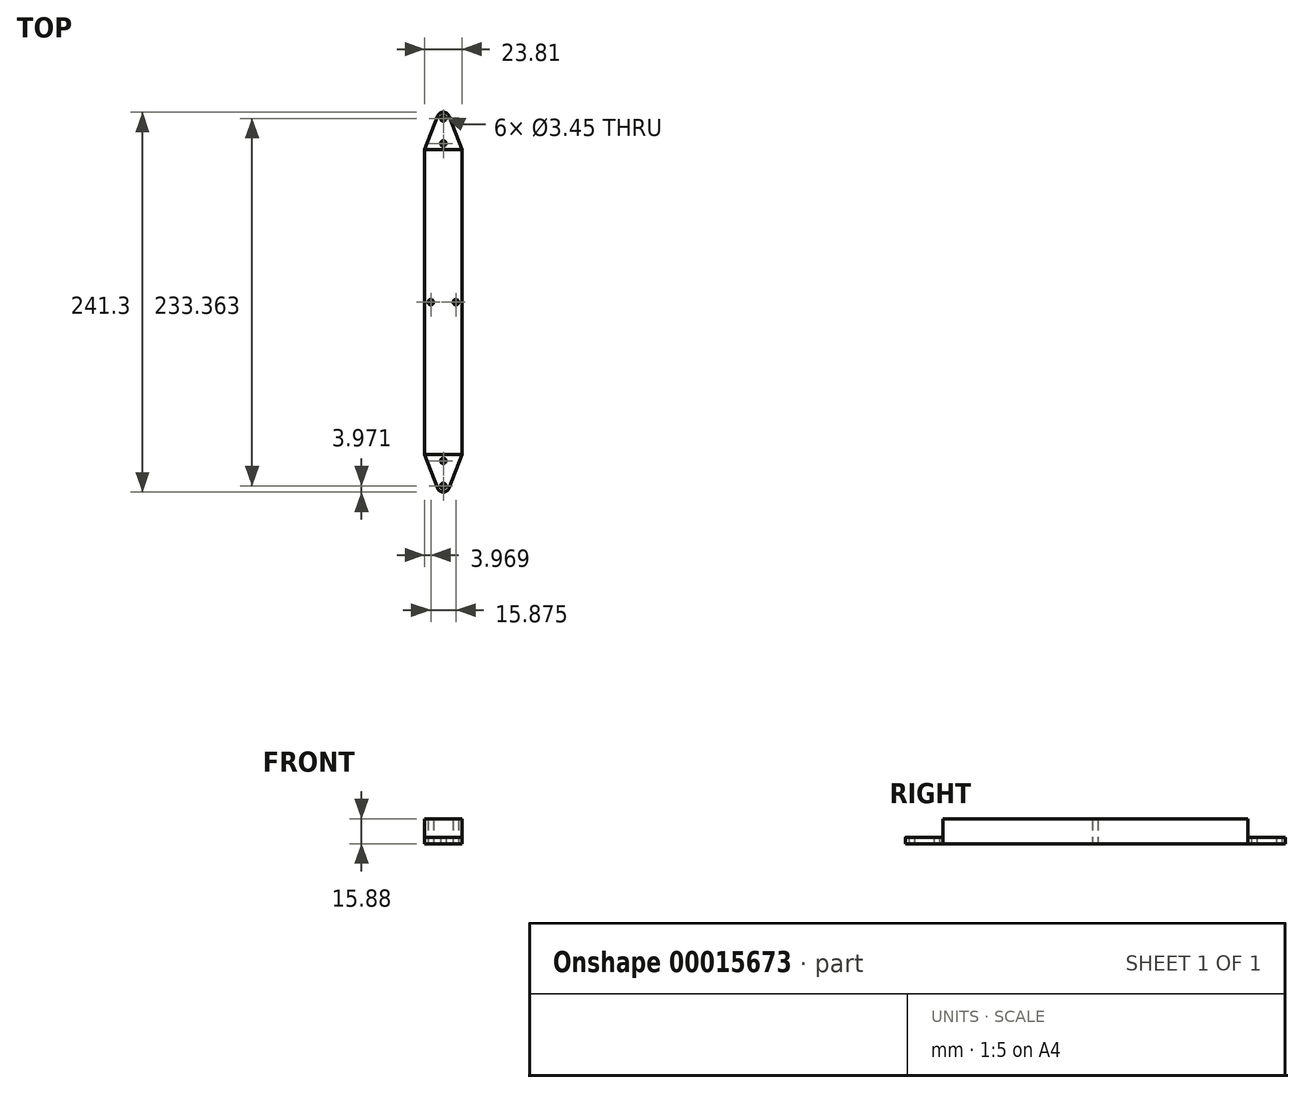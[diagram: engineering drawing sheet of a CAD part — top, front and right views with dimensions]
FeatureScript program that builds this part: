
annotation { "Feature Type Name" : "Feature", "Feature Type Description" : "" }
export const myFeature = defineFeature(function(context is Context, id is Id, definition is map)
    precondition{}
    {
        {
            var Q0;
            Q0=qCreatedBy(makeId("Top.planeOp"),FACE);
            var sketch = newSketch(context, id + "F0", { "sketchPlane" : qUnion([Q0])});
            skLineSegment(sketch, "E0.bottom", {"start": v(0, 0) * mm, "end": v(23.81, 0) * mm, "construction": true});
            skLineSegment(sketch, "E0.top", {"start": v(0, -193.68) * mm, "end": v(23.81, -193.68) * mm, "construction": true});
            skLineSegment(sketch, "E0.left", {"start": v(0, 0) * mm, "end": v(0, -193.68) * mm});
            skLineSegment(sketch, "E0.right", {"start": v(23.81, 0) * mm, "end": v(23.81, -193.68) * mm});
            skLineSegment(sketch, "E1", {"start": v(0, -96.84) * mm, "end": v(3.97, -96.84) * mm});
            skLineSegment(sketch, "E2", {"start": v(3.97, -96.84) * mm, "end": v(11.9, -96.84) * mm});
            skLineSegment(sketch, "E3", {"start": v(11.9, -96.84) * mm, "end": v(19.84, -96.84) * mm, "construction": true});
            skLineSegment(sketch, "E4", {"start": v(19.84, -96.84) * mm, "end": v(23.81, -96.84) * mm, "construction": true});
            skCircle(sketch, "E5", {"center": v(3.97, -96.84) * mm, "radius": 1.73 * mm});
            skCircle(sketch, "E6", {"center": v(19.84, -96.84) * mm, "radius": 1.73 * mm});
            skLineSegment(sketch, "E7", {"start": v(11.9, -193.68) * mm, "end": v(11.9, -197.64) * mm});
            skLineSegment(sketch, "E8", {"start": v(11.9, -197.64) * mm, "end": v(11.9, -205.58) * mm});
            skLineSegment(sketch, "E9", {"start": v(11.9, -205.58) * mm, "end": v(11.9, -213.52) * mm});
            skLineSegment(sketch, "E10", {"start": v(11.9, -213.52) * mm, "end": v(11.9, -217.49) * mm});
            skLineSegment(sketch, "E11", {"start": v(0, -193.68) * mm, "end": v(8.2, -214.95) * mm});
            skLineSegment(sketch, "E12", {"start": v(23.81, -193.68) * mm, "end": v(15.6, -214.95) * mm});
            skArc(sketch, "E13", {"start": v(8.2, -214.95) * mm, "mid": v(11.9, -217.49) * mm, "end": v(15.6, -214.95) * mm});
            skCircle(sketch, "E14", {"center": v(11.9, -213.52) * mm, "radius": 1.73 * mm});
            skCircle(sketch, "E15", {"center": v(11.9, -197.64) * mm, "radius": 1.73 * mm});
            skLineSegment(sketch, "E16", {"start": v(11.9, 0) * mm, "end": v(11.9, 3.97) * mm, "construction": true});
            skLineSegment(sketch, "E17", {"start": v(11.9, 3.97) * mm, "end": v(11.9, 11.9) * mm, "construction": true});
            skLineSegment(sketch, "E18", {"start": v(11.9, 11.9) * mm, "end": v(11.9, 19.84) * mm, "construction": true});
            skLineSegment(sketch, "E19", {"start": v(11.9, 19.84) * mm, "end": v(11.9, 23.81) * mm, "construction": true});
            skArc(sketch, "E20", {"start": v(15.6, 21.27) * mm, "mid": v(11.9, 23.81) * mm, "end": v(8.2, 21.27) * mm});
            skLineSegment(sketch, "E21", {"start": v(0, 0) * mm, "end": v(8.2, 21.27) * mm});
            skLineSegment(sketch, "E22", {"start": v(15.6, 21.27) * mm, "end": v(23.81, 0) * mm});
            skCircle(sketch, "E23", {"center": v(11.9, 19.84) * mm, "radius": 1.73 * mm});
            skCircle(sketch, "E24", {"center": v(11.9, 3.97) * mm, "radius": 1.73 * mm});
            skSolve(sketch);
        }
        {
            var Q0;
            Q0 = qSketchRegion(id + "F0", true);
            extrude(context, id + "F1", {"entities" : qUnion([Q0]), "depth" : 3.97 * mm});
        }
        {
            var Q0;
            Q0=makeQuery(id+"F1.opExtrude","CAP_FACE",FACE,{"disambiguationData":[OSD([sQuery(id+"F0.wireOp",EDGE,"E0.left"),sQuery(id+"F0.wireOp",EDGE,"E0.right"),sQuery(id+"F0.wireOp",EDGE,"E5"),sQuery(id+"F0.wireOp",EDGE,"E6"),sQuery(id+"F0.wireOp",EDGE,"E11"),sQuery(id+"F0.wireOp",EDGE,"E12"),sQuery(id+"F0.wireOp",EDGE,"E13"),sQuery(id+"F0.wireOp",EDGE,"E14"),sQuery(id+"F0.wireOp",EDGE,"E15"),sQuery(id+"F0.wireOp",EDGE,"E20"),sQuery(id+"F0.wireOp",EDGE,"E21"),sQuery(id+"F0.wireOp",EDGE,"E22"),sQuery(id+"F0.wireOp",EDGE,"E23"),sQuery(id+"F0.wireOp",EDGE,"E24")])],"isStart":false});
            var sketch = newSketch(context, id + "F2", { "sketchPlane" : qUnion([Q0])});
            skLineSegment(sketch, "E25.bottom", {"start": v(0, -193.68) * mm, "end": v(23.81, -193.68) * mm});
            skLineSegment(sketch, "E25.top", {"start": v(0, 0) * mm, "end": v(23.81, 0) * mm});
            skLineSegment(sketch, "E25.left", {"start": v(0, -193.68) * mm, "end": v(0, 0) * mm});
            skLineSegment(sketch, "E25.right", {"start": v(23.81, -193.68) * mm, "end": v(23.81, 0) * mm});
            skSolve(sketch);
        }
        {
            var Q0;
            Q0=makeQuery(id+"F2.imprint","IMPRINT",FACE,{"disambiguationData":[TD([[makeQuery(id+"F2.imprint","IMPRINT",EDGE,{"derivedFrom":sQuery(id+"F2.wireOp",EDGE,"E25.bottom")}),1.0]])]});
            extrude(context, id + "F3", {"entities" : qUnion([Q0]), "operationType" : NewBodyOperationType.ADD, "depth" : 11.9 * mm});
        }
    });
